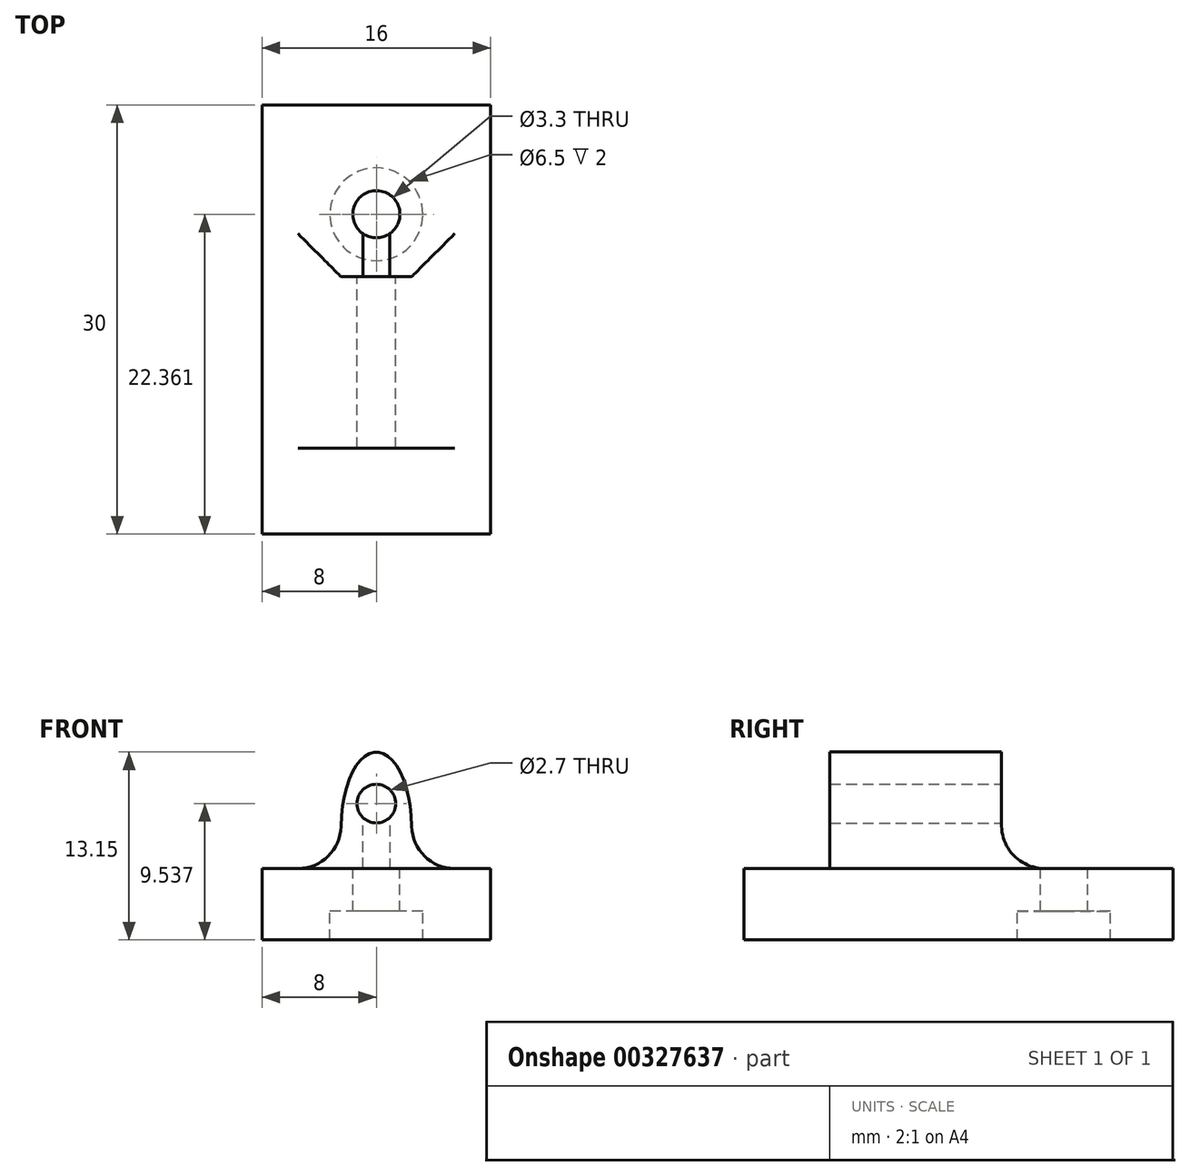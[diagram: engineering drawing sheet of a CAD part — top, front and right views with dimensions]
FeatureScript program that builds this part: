
annotation { "Feature Type Name" : "Feature", "Feature Type Description" : "" }
export const myFeature = defineFeature(function(context is Context, id is Id, definition is map)
    precondition{}
    {
        {
            var Q0;
            Q0=qCreatedBy(makeId("Top.planeOp"),FACE);
            var sketch = newSketch(context, id + "F0", { "sketchPlane" : qUnion([Q0])});
            skLineSegment(sketch, "E0.bottom", {"start": v(8, 15) * mm, "end": v(-8, 15) * mm});
            skLineSegment(sketch, "E0.top", {"start": v(8, -15) * mm, "end": v(-8, -15) * mm});
            skLineSegment(sketch, "E0.left", {"start": v(8, 15) * mm, "end": v(8, -15) * mm});
            skLineSegment(sketch, "E0.right", {"start": v(-8, 15) * mm, "end": v(-8, -15) * mm});
            skPoint(sketch, "E0.middle", {"position": v(0, 0) * mm});
            skPoint(sketch, "E1", {"position": v(0, 7.36) * mm});
            skSolve(sketch);
        }
        {
            var Q0;
            Q0 = qSketchRegion(id + "F0", true);
            extrude(context, id + "F1", {"entities" : qUnion([Q0]), "depth" : 5 * mm});
        }
        {
            var Q0;
            Q0=makeQuery(id+"F1.opExtrude","SWEPT_FACE",FACE,{"disambiguationData":[OSD([sQuery(id+"F0.wireOp",EDGE,"E0.top")])]});
            cPlane(context, id + "F2", {"entities" : qUnion([Q0]), "cplaneType" : CPlaneType.OFFSET, "offset" : 6 * mm, "oppositeDirection" : true, "width" : 150 * mm, "height" : 150 * mm});
        }
        {
            var Q0;
            Q0=qCreatedBy(id+"F2.planeOp",FACE);
            var sketch = newSketch(context, id + "F3", { "sketchPlane" : qUnion([Q0])});
            skEllipse(sketch, "E2", {"center": v(0, 7.75) * mm, "majorRadius": 5.4 * mm, "minorRadius": 2.48 * mm, "majorAxis": v(0, 1)});
            skSolve(sketch);
        }
        {
            var Q0;
            Q0 = qSketchRegion(id + "F3", true);
            extrude(context, id + "F4", {"entities" : qUnion([Q0]), "operationType" : NewBodyOperationType.ADD, "oppositeDirection" : true, "depth" : 12 * mm});
        }
        {
            var Q0;
            Q0=makeQuery(id+"F4.opExtrude","CAP_FACE",FACE,{"disambiguationData":[OSD([sQuery(id+"F3.wireOp",EDGE,"E2")])],"isStart":true});
            var sketch = newSketch(context, id + "F5", { "sketchPlane" : qUnion([Q0])});
            skPoint(sketch, "E3", {"position": v(0, 9.54) * mm});
            skSolve(sketch);
        }
        {
            var Q0;
            Q0=sQuery(id+"F5.wireOp",VERTEX,"E3");
            var Q1;
            Q1=makeQuery(id+"F1.opExtrude","SWEPT_BODY",BODY,{"disambiguationData":[OSD([sQuery(id+"F0.wireOp",EDGE,"E0.bottom"),sQuery(id+"F0.wireOp",EDGE,"E0.top"),sQuery(id+"F0.wireOp",EDGE,"E0.left"),sQuery(id+"F0.wireOp",EDGE,"E0.right")])]});
            hole(context, id + "F6", {"style" : HoleStyle.SIMPLE, "endStyle" : HoleEndStyle.THROUGH, "holeDiameter" : 2.7 * mm, "tappedDepth" : 12 * mm, "tapClearance" : 3, "startFromSketch" : true, "locations" : qUnion([Q0]), "scope" : qUnion([Q1])});
        }
        {
            var Q0;
            Q0=sQuery(id+"F0.wireOp",VERTEX,"E1");
            var Q1;
            Q1=makeQuery(id+"F1.opExtrude","SWEPT_BODY",BODY,{"disambiguationData":[OSD([sQuery(id+"F0.wireOp",EDGE,"E0.bottom"),sQuery(id+"F0.wireOp",EDGE,"E0.top"),sQuery(id+"F0.wireOp",EDGE,"E0.left"),sQuery(id+"F0.wireOp",EDGE,"E0.right")])]});
            hole(context, id + "F7", {"style" : HoleStyle.C_BORE, "endStyle" : HoleEndStyle.THROUGH, "oppositeDirection" : true, "holeDiameter" : 3.3 * mm, "cBoreDiameter" : 6.5 * mm, "cBoreDepth" : 2 * mm, "tappedDepth" : 12 * mm, "tapClearance" : 3, "startFromSketch" : true, "locations" : qUnion([Q0]), "scope" : qUnion([Q1])});
        }
        {
            var Q0;
            Q0=makeQuery(id+"F4.boolean.opBoolean","INTERSECT",EDGE,{"disambiguationData":[OD(1.0)],"derivedFrom":[makeQuery(id+"F1.opExtrude","CAP_FACE",FACE,{"disambiguationData":[OSD([sQuery(id+"F0.wireOp",EDGE,"E0.bottom"),sQuery(id+"F0.wireOp",EDGE,"E0.top"),sQuery(id+"F0.wireOp",EDGE,"E0.left"),sQuery(id+"F0.wireOp",EDGE,"E0.right")])],"isStart":false}),makeQuery(id+"F4.opExtrude","SWEPT_FACE",FACE,{"disambiguationData":[OSD([sQuery(id+"F3.wireOp",EDGE,"E2")])]})]});
            var Q1;
            Q1=makeQuery(id+"F4.boolean.opBoolean","INTERSECT",EDGE,{"disambiguationData":[OD(0.0)],"derivedFrom":[makeQuery(id+"F1.opExtrude","CAP_FACE",FACE,{"disambiguationData":[OSD([sQuery(id+"F0.wireOp",EDGE,"E0.bottom"),sQuery(id+"F0.wireOp",EDGE,"E0.top"),sQuery(id+"F0.wireOp",EDGE,"E0.left"),sQuery(id+"F0.wireOp",EDGE,"E0.right")])],"isStart":false}),makeQuery(id+"F4.opExtrude","SWEPT_FACE",FACE,{"disambiguationData":[OSD([sQuery(id+"F3.wireOp",EDGE,"E2")])]})]});
            var Q2;
            Q2=makeQuery(id+"F4.boolean.opBoolean","INTERSECT",EDGE,{"derivedFrom":[makeQuery(id+"F1.opExtrude","CAP_FACE",FACE,{"disambiguationData":[OSD([sQuery(id+"F0.wireOp",EDGE,"E0.bottom"),sQuery(id+"F0.wireOp",EDGE,"E0.top"),sQuery(id+"F0.wireOp",EDGE,"E0.left"),sQuery(id+"F0.wireOp",EDGE,"E0.right")])],"isStart":false}),makeQuery(id+"F4.opExtrude","CAP_FACE",FACE,{"disambiguationData":[OSD([sQuery(id+"F3.wireOp",EDGE,"E2")])],"isStart":false})]});
            fillet(context, id + "F8", {"entities" : qUnion([Q0, Q1, Q2]), "radius" : 3 * mm, "tangentPropagation" : true, "allowEdgeOverflow" : false});
        }
    });
